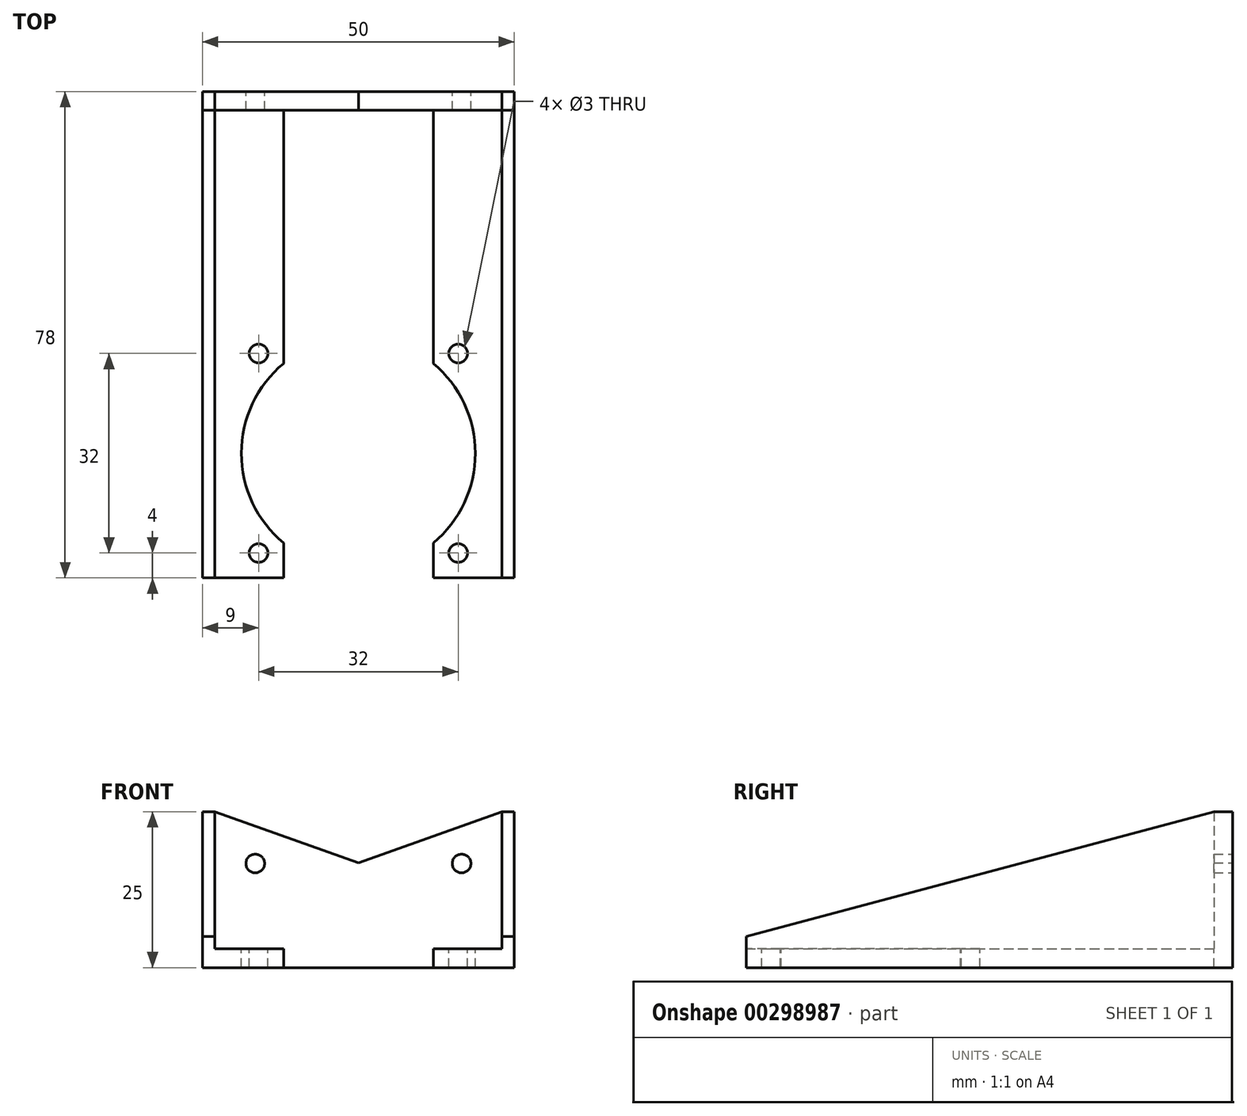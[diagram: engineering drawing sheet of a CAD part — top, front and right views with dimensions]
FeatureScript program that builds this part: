
annotation { "Feature Type Name" : "Feature", "Feature Type Description" : "" }
export const myFeature = defineFeature(function(context is Context, id is Id, definition is map)
    precondition{}
    {
        {
            var Q0;
            Q0=qCreatedBy(makeId("Top.planeOp"),FACE);
            var sketch = newSketch(context, id + "F0", { "sketchPlane" : qUnion([Q0])});
            skLineSegment(sketch, "E0.bottom", {"start": v(0, 0) * mm, "end": v(40, 0) * mm, "construction": true});
            skLineSegment(sketch, "E0.top", {"start": v(0, 40) * mm, "end": v(40, 40) * mm, "construction": true});
            skLineSegment(sketch, "E0.left", {"start": v(0, 0) * mm, "end": v(0, 40) * mm, "construction": true});
            skLineSegment(sketch, "E0.right", {"start": v(40, 0) * mm, "end": v(40, 40) * mm, "construction": true});
            skLineSegment(sketch, "E1", {"start": v(0, 78) * mm, "end": v(40, 78) * mm, "construction": true});
            skLineSegment(sketch, "E2", {"start": v(20, 40) * mm, "end": v(20, 0) * mm, "construction": true});
            skLineSegment(sketch, "E3", {"start": v(0, 20) * mm, "end": v(40, 20) * mm, "construction": true});
            skCircle(sketch, "E4", {"center": v(4, 36) * mm, "radius": 1.5 * mm});
            skCircle(sketch, "E5.MirrorC", {"center": v(36, 36) * mm, "radius": 1.5 * mm});
            skCircle(sketch, "E6.MirrorC", {"center": v(4, 4) * mm, "radius": 1.5 * mm});
            skCircle(sketch, "E7.MirrorC", {"center": v(36, 4) * mm, "radius": 1.5 * mm});
            skCircle(sketch, "E8", {"center": v(20, 20) * mm, "radius": 18.75 * mm, "construction": true});
            skLineSegment(sketch, "E9", {"start": v(8, 5.6) * mm, "end": v(8, 0) * mm});
            skLineSegment(sketch, "E10", {"start": v(8, 0) * mm, "end": v(-3, 0) * mm});
            skLineSegment(sketch, "E11", {"start": v(-3, 0) * mm, "end": v(-3, 78) * mm});
            skLineSegment(sketch, "E12", {"start": v(-3, 78) * mm, "end": v(20, 78) * mm});
            skArc(sketch, "E13", {"start": v(8, 5.6) * mm, "mid": v(1.25, 20) * mm, "end": v(8, 34.4) * mm});
            skLineSegment(sketch, "E14", {"start": v(8, 34.4) * mm, "end": v(8, 75) * mm});
            skLineSegment(sketch, "E15", {"start": v(8, 75) * mm, "end": v(20, 75) * mm});
            skLineSegment(sketch, "E16.MirrorCS", {"start": v(43, 78) * mm, "end": v(20, 78) * mm});
            skLineSegment(sketch, "E17.MirrorCS", {"start": v(43, 0) * mm, "end": v(43, 78) * mm});
            skLineSegment(sketch, "E18.MirrorCS", {"start": v(40, 0) * mm, "end": v(0, 0) * mm, "construction": true});
            skArc(sketch, "E19.MirrorCS", {"start": v(32, 5.6) * mm, "mid": v(38.75, 20) * mm, "end": v(32, 34.4) * mm});
            skLineSegment(sketch, "E20.MirrorCS", {"start": v(32, 34.4) * mm, "end": v(32, 75) * mm});
            skLineSegment(sketch, "E21.MirrorCS", {"start": v(40, 40) * mm, "end": v(0, 40) * mm, "construction": true});
            skLineSegment(sketch, "E22.MirrorCS", {"start": v(32, 0) * mm, "end": v(43, 0) * mm});
            skLineSegment(sketch, "E23.MirrorCS", {"start": v(32, 75) * mm, "end": v(20, 75) * mm});
            skLineSegment(sketch, "E24.MirrorCS", {"start": v(32, 5.6) * mm, "end": v(32, 0) * mm});
            skLineSegment(sketch, "E25.MirrorCS", {"start": v(40, 78) * mm, "end": v(0, 78) * mm, "construction": true});
            skLineSegment(sketch, "E26.MirrorCS", {"start": v(40, 20) * mm, "end": v(0, 20) * mm, "construction": true});
            skSolve(sketch);
        }
        {
            var Q0;
            Q0 = qSketchRegion(id + "F0", true);
            extrude(context, id + "F1", {"entities" : qUnion([Q0]), "oppositeDirection" : true, "depth" : 3 * mm});
        }
        {
            var Q0;
            Q0=makeQuery(id+"F1.opExtrude","SWEPT_FACE",FACE,{"disambiguationData":[OSD([sQuery(id+"F0.wireOp",EDGE,"E11")])]});
            var sketch = newSketch(context, id + "F2", { "sketchPlane" : qUnion([Q0])});
            skLineSegment(sketch, "E27", {"start": v(0, -3) * mm, "end": v(0, 2) * mm});
            skLineSegment(sketch, "E28.0", {"start": v(0, -3) * mm, "end": v(-78, -3) * mm});
            skLineSegment(sketch, "E29", {"start": v(-78, -3) * mm, "end": v(-78, 22) * mm});
            skPoint(sketch, "E30.0", {"position": v(-75, 0) * mm});
            skLineSegment(sketch, "E31", {"start": v(-78, 22) * mm, "end": v(-75, 22) * mm});
            skLineSegment(sketch, "E32", {"start": v(-75, 22) * mm, "end": v(0, 2) * mm});
            skSolve(sketch);
        }
        {
            var Q0;
            Q0 = qSketchRegion(id + "F2", true);
            extrude(context, id + "F3", {"entities" : qUnion([Q0]), "operationType" : NewBodyOperationType.ADD, "depth" : 2 * mm});
        }
        {
            var Q0;
            Q0=sQuery(id+"F0.wireOp",EDGE,"E26.MirrorCS");
            cPoint(context, id + "F4", {"entities" : qUnion([Q0]), "parameter" : 0.5});
        }
        {
            var Q0;
            Q0=qCreatedBy(makeId("Right.planeOp"),FACE);
            var Q1;
            Q1 = qCreatedBy(id + "F4" ,VERTEX);
            cPlane(context, id + "F5", {"entities" : qUnion([Q0, Q1]), "cplaneType" : CPlaneType.PLANE_POINT, "offset" : 25 * mm, "width" : 150 * mm, "height" : 150 * mm});
        }
        {
            var Q0;
            Q0=makeQuery(id+"F1.opExtrude","SWEPT_BODY",BODY,{"disambiguationData":[OSD([sQuery(id+"F0.wireOp",EDGE,"E4"),sQuery(id+"F0.wireOp",EDGE,"E6.MirrorC"),sQuery(id+"F0.wireOp",EDGE,"E9"),sQuery(id+"F0.wireOp",EDGE,"E10"),sQuery(id+"F0.wireOp",EDGE,"E11"),sQuery(id+"F0.wireOp",EDGE,"E12"),sQuery(id+"F0.wireOp",EDGE,"E13"),sQuery(id+"F0.wireOp",EDGE,"E14"),sQuery(id+"F0.wireOp",EDGE,"E15"),sQuery(id+"F0.wireOp",EDGE,"E16.MirrorCS"),sQuery(id+"F0.wireOp",EDGE,"E17.MirrorCS"),sQuery(id+"F0.wireOp",EDGE,"E19.MirrorCS"),sQuery(id+"F0.wireOp",EDGE,"E20.MirrorCS"),sQuery(id+"F0.wireOp",EDGE,"E22.MirrorCS"),sQuery(id+"F0.wireOp",EDGE,"E23.MirrorCS"),sQuery(id+"F0.wireOp",EDGE,"E24.MirrorCS"),sQuery(id+"F0.wireOp",EDGE,"E5.MirrorC"),sQuery(id+"F0.wireOp",EDGE,"E7.MirrorC")])]});
            var Q1;
            Q1=qCreatedBy(id+"F5.planeOp",FACE);
            mirror(context, id + "F6", {"operationType" : NewBodyOperationType.ADD, "entities" : qUnion([Q0]), "mirrorPlane" : qUnion([Q1])});
        }
        {
            var Q0;
            {var subQ0=makeQuery(id+"F3.boolean.opBoolean","MERGE",FACE,{"derivedFrom":[makeQuery(id+"F1.opExtrude","SWEPT_FACE",FACE,{"disambiguationData":[OSD([sQuery(id+"F0.wireOp",EDGE,"E12"),sQuery(id+"F0.wireOp",EDGE,"E16.MirrorCS")])]}),makeQuery(id+"F3.opExtrude","SWEPT_FACE",FACE,{"disambiguationData":[OSD([sQuery(id+"F2.wireOp",EDGE,"E29")])]})]});Q0=makeQuery(id+"F6.boolean.opBoolean","MERGE",FACE,{"derivedFrom":[subQ0,makeQuery(id+"F6.opPattern","COPY",FACE,{"derivedFrom":subQ0,"instanceName":"1"})]});}
            var sketch = newSketch(context, id + "F7", { "sketchPlane" : qUnion([Q0])});
            skLineSegment(sketch, "E33.0", {"start": v(-45, -3) * mm, "end": v(-45, 22) * mm});
            skLineSegment(sketch, "E34.0", {"start": v(-45, -3) * mm, "end": v(5, -3) * mm});
            skLineSegment(sketch, "E35.0", {"start": v(5, -3) * mm, "end": v(5, 22) * mm});
            skCircle(sketch, "E36", {"center": v(-36.54, 13.7) * mm, "radius": 1.5 * mm});
            skCircle(sketch, "E37.MirrorC", {"center": v(-3.46, 13.7) * mm, "radius": 1.5 * mm});
            skLineSegment(sketch, "E38.0", {"start": v(-45, 22) * mm, "end": v(-43, 22) * mm});
            skLineSegment(sketch, "E39.0", {"start": v(5, 22) * mm, "end": v(3, 22) * mm});
            skLineSegment(sketch, "E40", {"start": v(-43, 22) * mm, "end": v(-20, 13.8) * mm});
            skPoint(sketch, "E40.endSnap0", {"position": v(-20, 0) * mm});
            skLineSegment(sketch, "E41", {"start": v(-20, 13.8) * mm, "end": v(3, 22) * mm});
            skSolve(sketch);
        }
        {
            var Q0;
            Q0 = qSketchRegion(id + "F7", true);
            var Q1;
            Q1=makeQuery(id+"F1.opExtrude","SWEPT_FACE",FACE,{"disambiguationData":[OSD([sQuery(id+"F0.wireOp",EDGE,"E15"),sQuery(id+"F0.wireOp",EDGE,"E23.MirrorCS")])]});
            extrude(context, id + "F8", {"entities" : qUnion([Q0]), "operationType" : NewBodyOperationType.ADD, "endBound" : BoundingType.UP_TO_SURFACE, "oppositeDirection" : true, "endBoundEntityFace" : qUnion([Q1]), "depth" : 25 * mm});
        }
    });
